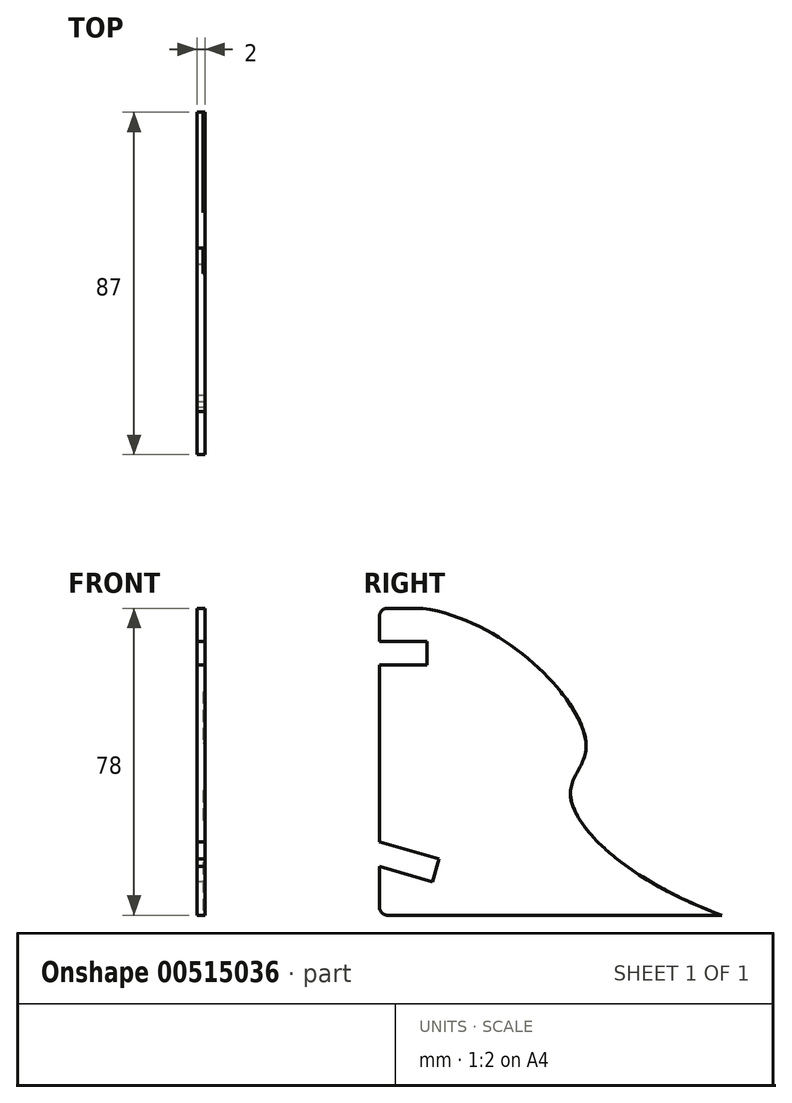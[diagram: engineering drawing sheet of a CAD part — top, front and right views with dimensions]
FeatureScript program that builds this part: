
annotation { "Feature Type Name" : "Feature", "Feature Type Description" : "" }
export const myFeature = defineFeature(function(context is Context, id is Id, definition is map)
    precondition{}
    {
        {
            var Q0;
            Q0=qCreatedBy(makeId("Right.planeOp"),FACE);
            var sketch = newSketch(context, id + "F0", { "sketchPlane" : qUnion([Q0])});
            skLineSegment(sketch, "E0", {"start": v(2, 78) * mm, "end": v(42, 78) * mm});
            skLineSegment(sketch, "E1", {"start": v(2, 0) * mm, "end": v(109, 0) * mm});
            skLineSegment(sketch, "E2", {"start": v(0, 76) * mm, "end": v(0, 69.6) * mm});
            skLineSegment(sketch, "E3", {"start": v(0, 69.6) * mm, "end": v(12, 69.6) * mm});
            skLineSegment(sketch, "E4", {"start": v(12, 69.6) * mm, "end": v(12, 63.6) * mm});
            skLineSegment(sketch, "E5", {"start": v(12, 63.6) * mm, "end": v(0, 63.6) * mm});
            skLineSegment(sketch, "E6", {"start": v(0, 63.6) * mm, "end": v(0, 18.6) * mm});
            skLineSegment(sketch, "E7", {"start": v(0, 18.6) * mm, "end": v(15.11, 14.26) * mm});
            skLineSegment(sketch, "E8", {"start": v(15.11, 14.26) * mm, "end": v(13.46, 8.5) * mm});
            skLineSegment(sketch, "E9", {"start": v(13.46, 8.5) * mm, "end": v(0, 12.35) * mm});
            skLineSegment(sketch, "E10", {"start": v(0, 12.35) * mm, "end": v(0, 2) * mm});
            skPoint(sketch, "E11.visualSharp", {"position": v(0, 78) * mm});
            skArc(sketch, "E11.filletArc", {"start": v(2, 78) * mm, "mid": v(0.59, 77.41) * mm, "end": v(0, 76) * mm});
            skPoint(sketch, "E12.visualSharp", {"position": v(0, 0) * mm});
            skArc(sketch, "E12.filletArc", {"start": v(0, 2) * mm, "mid": v(0.59, 0.59) * mm, "end": v(2, 0) * mm});
            skFitSpline(sketch, "E13", {"points": [v(42, 78) * mm, v(52.9, 71.65) * mm, v(140, 18) * mm, v(109, 0) * mm], "startDerivative": vector(128.82, -58.6) * mm, "endDerivative": vector(-133.84, -23.06) * mm});
            skSolve(sketch);
        }
        {
            var Q0;
            Q0=qSketchRegion(id+"F0",true);
            extrude(context, id + "F1", {"entities" : qUnion([Q0]), "depth" : 1.5 * mm});
        }
        {
            var Q0;
            Q0=makeQuery(id+"F1.opExtrude","CAP_FACE",FACE,{"disambiguationData":[OSD([sQuery(id+"F0.wireOp",EDGE,"E0"),sQuery(id+"F0.wireOp",EDGE,"E1"),sQuery(id+"F0.wireOp",EDGE,"E2"),sQuery(id+"F0.wireOp",EDGE,"E3"),sQuery(id+"F0.wireOp",EDGE,"E4"),sQuery(id+"F0.wireOp",EDGE,"E5"),sQuery(id+"F0.wireOp",EDGE,"E6"),sQuery(id+"F0.wireOp",EDGE,"E7"),sQuery(id+"F0.wireOp",EDGE,"E8"),sQuery(id+"F0.wireOp",EDGE,"E9"),sQuery(id+"F0.wireOp",EDGE,"E10"),sQuery(id+"F0.wireOp",EDGE,"E11.filletArc"),sQuery(id+"F0.wireOp",EDGE,"E12.filletArc"),sQuery(id+"F0.wireOp",EDGE,"E13")])],"isStart":false});
            var sketch = newSketch(context, id + "F2", { "sketchPlane" : qUnion([Q0])});
            skSolve(sketch);
        }
        {
            var Q0;
            Q0=makeQuery(id+"F2.imprint","IMPRINT",FACE,{"disambiguationData":[TD([[makeQuery(id+"F2.imprint","IMPRINT",EDGE,{"derivedFrom":makeQuery(id+"F1.opExtrude","CAP_EDGE",EDGE,{"disambiguationData":[OSD([sQuery(id+"F0.wireOp",EDGE,"E0")])],"isStart":false})}),-1.0]])]});
            var sketch = newSketch(context, id + "F3", { "sketchPlane" : qUnion([Q0])});
            skLineSegment(sketch, "E14", {"start": v(11, 0) * mm, "end": v(11, 78) * mm, "construction": true});
            skFitSpline(sketch, "E15", {"points": [v(11, 78) * mm, v(52.5, 43) * mm, v(48.5, 31.5) * mm, v(87, 0) * mm], "startDerivative": vector(166.3, -24.45) * mm, "endDerivative": vector(190.57, -69.04) * mm});
            skLineSegment(sketch, "E16", {"start": v(11, 78) * mm, "end": v(2, 78) * mm});
            skLineSegment(sketch, "E17", {"start": v(0, 76) * mm, "end": v(0, 2) * mm});
            skLineSegment(sketch, "E18", {"start": v(2, 0) * mm, "end": v(87, 0) * mm});
            skPoint(sketch, "E19.visualSharp", {"position": v(0, 78) * mm});
            skArc(sketch, "E19.filletArc", {"start": v(2, 78) * mm, "mid": v(0.59, 77.41) * mm, "end": v(0, 76) * mm});
            skPoint(sketch, "E20.visualSharp", {"position": v(0, 0) * mm});
            skArc(sketch, "E20.filletArc", {"start": v(0, 2) * mm, "mid": v(0.59, 0.59) * mm, "end": v(2, 0) * mm});
            skSolve(sketch);
        }
        {
            var Q0;
            Q0=qSketchRegion(id+"F3",true);
            extrude(context, id + "F4", {"entities" : qUnion([Q0]), "operationType" : NewBodyOperationType.ADD, "depth" : .5 * mm});
        }
        {
            var Q0;
            Q0=makeQuery(id+"F1.opExtrude","CAP_FACE",FACE,{"disambiguationData":[OSD([sQuery(id+"F0.wireOp",EDGE,"E0"),sQuery(id+"F0.wireOp",EDGE,"E1"),sQuery(id+"F0.wireOp",EDGE,"E2"),sQuery(id+"F0.wireOp",EDGE,"E3"),sQuery(id+"F0.wireOp",EDGE,"E4"),sQuery(id+"F0.wireOp",EDGE,"E5"),sQuery(id+"F0.wireOp",EDGE,"E6"),sQuery(id+"F0.wireOp",EDGE,"E7"),sQuery(id+"F0.wireOp",EDGE,"E8"),sQuery(id+"F0.wireOp",EDGE,"E9"),sQuery(id+"F0.wireOp",EDGE,"E10"),sQuery(id+"F0.wireOp",EDGE,"E11.filletArc"),sQuery(id+"F0.wireOp",EDGE,"E12.filletArc"),sQuery(id+"F0.wireOp",EDGE,"E13")])],"isStart":true});
            var sketch = newSketch(context, id + "F5", { "sketchPlane" : qUnion([Q0])});
            skLineSegment(sketch, "E21.bottom", {"start": v(-12, 69.6) * mm, "end": v(0, 69.6) * mm});
            skLineSegment(sketch, "E21.top", {"start": v(-12, 63.6) * mm, "end": v(0, 63.6) * mm});
            skLineSegment(sketch, "E21.left", {"start": v(-12, 69.6) * mm, "end": v(-12, 63.6) * mm});
            skLineSegment(sketch, "E21.right", {"start": v(0, 69.6) * mm, "end": v(0, 63.6) * mm});
            skLineSegment(sketch, "E22", {"start": v(0, 18.6) * mm, "end": v(-15.11, 14.26) * mm});
            skLineSegment(sketch, "E23", {"start": v(-15.11, 14.26) * mm, "end": v(-13.46, 8.5) * mm});
            skLineSegment(sketch, "E24", {"start": v(-13.46, 8.5) * mm, "end": v(0, 12.35) * mm});
            skLineSegment(sketch, "E25", {"start": v(0, 12.35) * mm, "end": v(0, 18.6) * mm});
            skSolve(sketch);
        }
        {
            var Q0;
            Q0=qSketchRegion(id+"F5",true);
            extrude(context, id + "F6", {"entities" : qUnion([Q0]), "operationType" : NewBodyOperationType.REMOVE, "oppositeDirection" : true, "depth" : 25 * mm});
        }
        {
            var Q0;
            Q0=makeQuery(id+"F1.opExtrude","CAP_FACE",FACE,{"disambiguationData":[OSD([sQuery(id+"F0.wireOp",EDGE,"E0"),sQuery(id+"F0.wireOp",EDGE,"E1"),sQuery(id+"F0.wireOp",EDGE,"E2"),sQuery(id+"F0.wireOp",EDGE,"E3"),sQuery(id+"F0.wireOp",EDGE,"E4"),sQuery(id+"F0.wireOp",EDGE,"E5"),sQuery(id+"F0.wireOp",EDGE,"E6"),sQuery(id+"F0.wireOp",EDGE,"E7"),sQuery(id+"F0.wireOp",EDGE,"E8"),sQuery(id+"F0.wireOp",EDGE,"E9"),sQuery(id+"F0.wireOp",EDGE,"E10"),sQuery(id+"F0.wireOp",EDGE,"E11.filletArc"),sQuery(id+"F0.wireOp",EDGE,"E12.filletArc"),sQuery(id+"F0.wireOp",EDGE,"E13")])],"isStart":false});
            var sketch = newSketch(context, id + "F7", { "sketchPlane" : qUnion([Q0])});
            skLineSegment(sketch, "E26", {"start": v(11, 78) * mm, "end": v(42, 78) * mm});
            skLineSegment(sketch, "E27", {"start": v(42, 78) * mm, "end": v(144.04, 78) * mm});
            skLineSegment(sketch, "E28", {"start": v(144.04, 78) * mm, "end": v(150.45, -1.8) * mm});
            skLineSegment(sketch, "E29", {"start": v(150.45, -1.8) * mm, "end": v(87, 0) * mm});
            skFitSpline(sketch, "E30", {"points": [v(11, 78) * mm, v(52.45, 43.76) * mm, v(48.52, 31.72) * mm, v(87, 0) * mm], "startDerivative": vector(159.44, -24.23) * mm, "endDerivative": vector(194.66, -71.72) * mm});
            skSolve(sketch);
        }
        {
            var Q0;
            Q0 = qSketchRegion(id + "F7", true);
            extrude(context, id + "F8", {"entities" : qUnion([Q0]), "operationType" : NewBodyOperationType.REMOVE, "oppositeDirection" : true, "depth" : 25 * mm, "hasSecondDirection" : true, "secondDirectionOppositeDirection" : false, "secondDirectionDepth" : 25 * mm});
        }
    });
